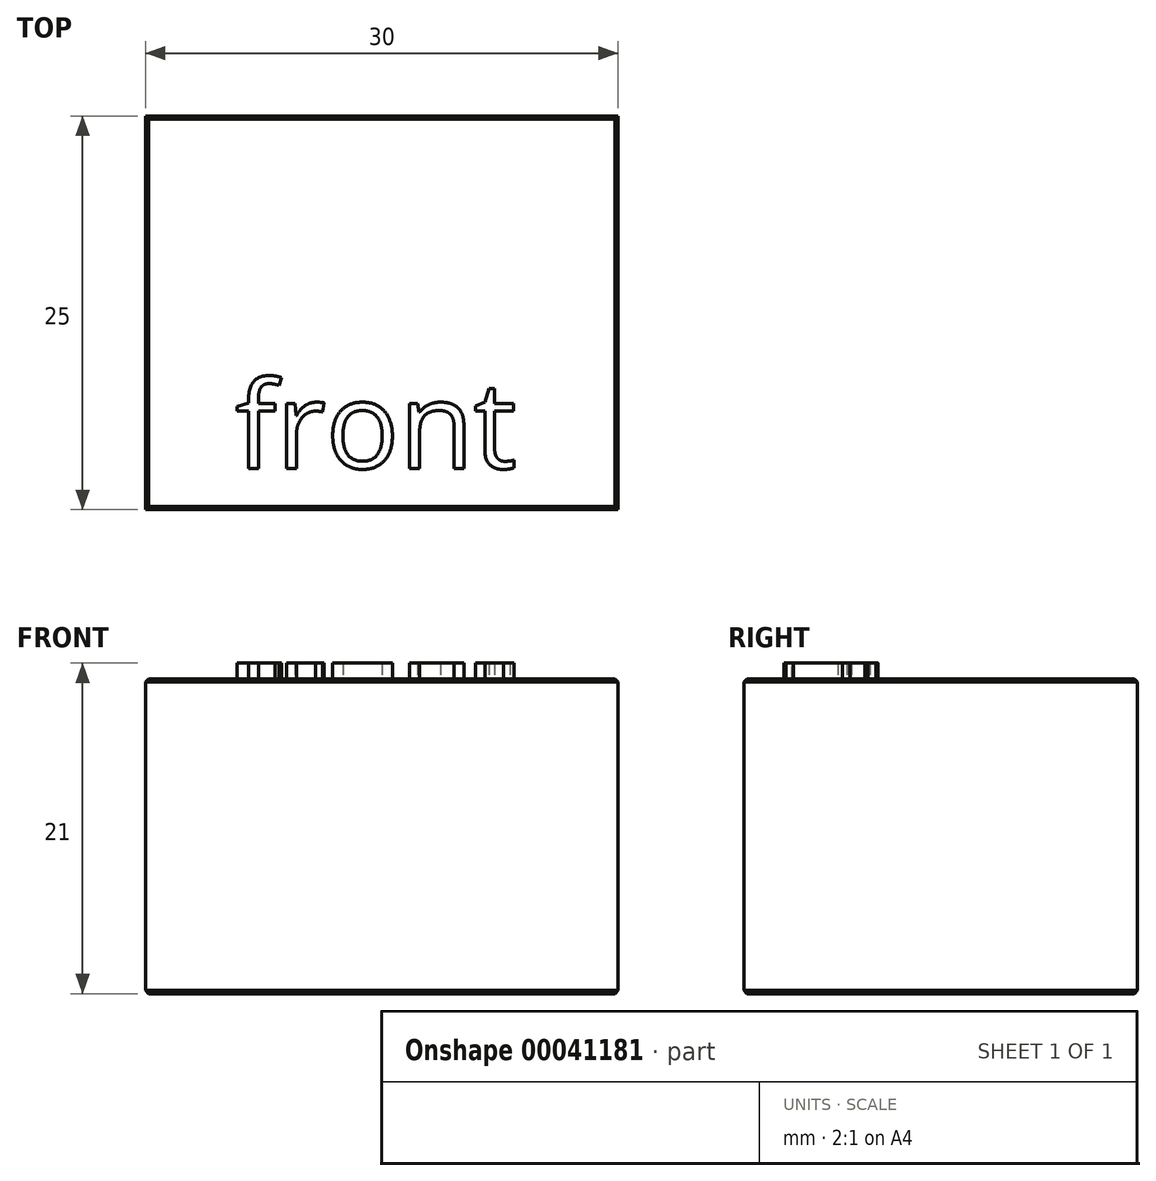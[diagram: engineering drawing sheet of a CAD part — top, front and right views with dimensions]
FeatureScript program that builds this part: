
annotation { "Feature Type Name" : "Feature", "Feature Type Description" : "" }
export const myFeature = defineFeature(function(context is Context, id is Id, definition is map)
    precondition{}
    {
        {
            var Q0;
            Q0=qCreatedBy(makeId("Top.planeOp"),FACE);
            var sketch = newSketch(context, id + "F0", { "sketchPlane" : qUnion([Q0])});
            skLineSegment(sketch, "E0.rect.bottom", {"start": v(15, 12.5) * mm, "end": v(-15, 12.5) * mm});
            skLineSegment(sketch, "E0.rect.top", {"start": v(15, -12.5) * mm, "end": v(-15, -12.5) * mm});
            skLineSegment(sketch, "E0.rect.left", {"start": v(15, 12.5) * mm, "end": v(15, -12.5) * mm});
            skLineSegment(sketch, "E0.rect.right", {"start": v(-15, 12.5) * mm, "end": v(-15, -12.5) * mm});
            skPoint(sketch, "E0.rect.middle", {"position": v(0, 0) * mm});
            skSolve(sketch);
        }
        {
            var Q0;
            Q0=makeQuery(id+"F0.imprint","IMPRINT",FACE,{"disambiguationData":[TD([[makeQuery(id+"F0.imprint","IMPRINT",EDGE,{"derivedFrom":sQuery(id+"F0.wireOp",EDGE,"E0.rect.bottom")}),1.0]])]});
            extrude(context, id + "F1", {"entities" : qUnion([Q0]), "depth" : 20 * mm});
        }
        {
            var Q0;
            Q0=makeQuery(id+"F1.opExtrude","CAP_EDGE",EDGE,{"disambiguationData":[OSD([sQuery(id+"F0.wireOp",EDGE,"E0.rect.top")])],"isStart":false});
            var Q1;
            Q1=makeQuery(id+"F1.opExtrude","CAP_EDGE",EDGE,{"disambiguationData":[OSD([sQuery(id+"F0.wireOp",EDGE,"E0.rect.right")])],"isStart":false});
            var Q2;
            Q2=makeQuery(id+"F1.opExtrude","CAP_EDGE",EDGE,{"disambiguationData":[OSD([sQuery(id+"F0.wireOp",EDGE,"E0.rect.bottom")])],"isStart":false});
            var Q3;
            Q3=makeQuery(id+"F1.opExtrude","CAP_EDGE",EDGE,{"disambiguationData":[OSD([sQuery(id+"F0.wireOp",EDGE,"E0.rect.left")])],"isStart":false});
            var Q4;
            Q4=makeQuery(id+"F1.opExtrude","CAP_EDGE",EDGE,{"disambiguationData":[OSD([sQuery(id+"F0.wireOp",EDGE,"E0.rect.top")])],"isStart":true});
            var Q5;
            Q5=makeQuery(id+"F1.opExtrude","CAP_EDGE",EDGE,{"disambiguationData":[OSD([sQuery(id+"F0.wireOp",EDGE,"E0.rect.right")])],"isStart":true});
            var Q6;
            Q6=makeQuery(id+"F1.opExtrude","CAP_EDGE",EDGE,{"disambiguationData":[OSD([sQuery(id+"F0.wireOp",EDGE,"E0.rect.bottom")])],"isStart":true});
            var Q7;
            Q7=makeQuery(id+"F1.opExtrude","CAP_EDGE",EDGE,{"disambiguationData":[OSD([sQuery(id+"F0.wireOp",EDGE,"E0.rect.left")])],"isStart":true});
            chamfer(context, id + "F2", {"entities" : qUnion([Q0, Q1, Q2, Q3, Q4, Q5, Q6, Q7]), "width" : .2 * mm, "tangentPropagation" : true});
        }
        {
            var Q0;
            Q0=makeQuery(id+"F1.opExtrude","CAP_FACE",FACE,{"disambiguationData":[OSD([sQuery(id+"F0.wireOp",EDGE,"E0.rect.bottom"),sQuery(id+"F0.wireOp",EDGE,"E0.rect.top"),sQuery(id+"F0.wireOp",EDGE,"E0.rect.left"),sQuery(id+"F0.wireOp",EDGE,"E0.rect.right")])],"isStart":false});
            var sketch = newSketch(context, id + "F3", { "sketchPlane" : qUnion([Q0])});
            skText(sketch, "E1", { "text": "front", "fontName": "OpenSans-Regular.ttf"});
            const initialGuessF3  = {"E1": [-0.00931, -0.00988, 1, 0, 0.00555]};
            skSetInitialGuess(sketch, initialGuessF3);
            skSolve(sketch);
        }
        {
            var Q0;
            Q0 = qSketchRegion(id + "F3", true);
            extrude(context, id + "F4", {"entities" : qUnion([Q0]), "operationType" : NewBodyOperationType.ADD, "depth" : 1 * mm});
        }
    });
